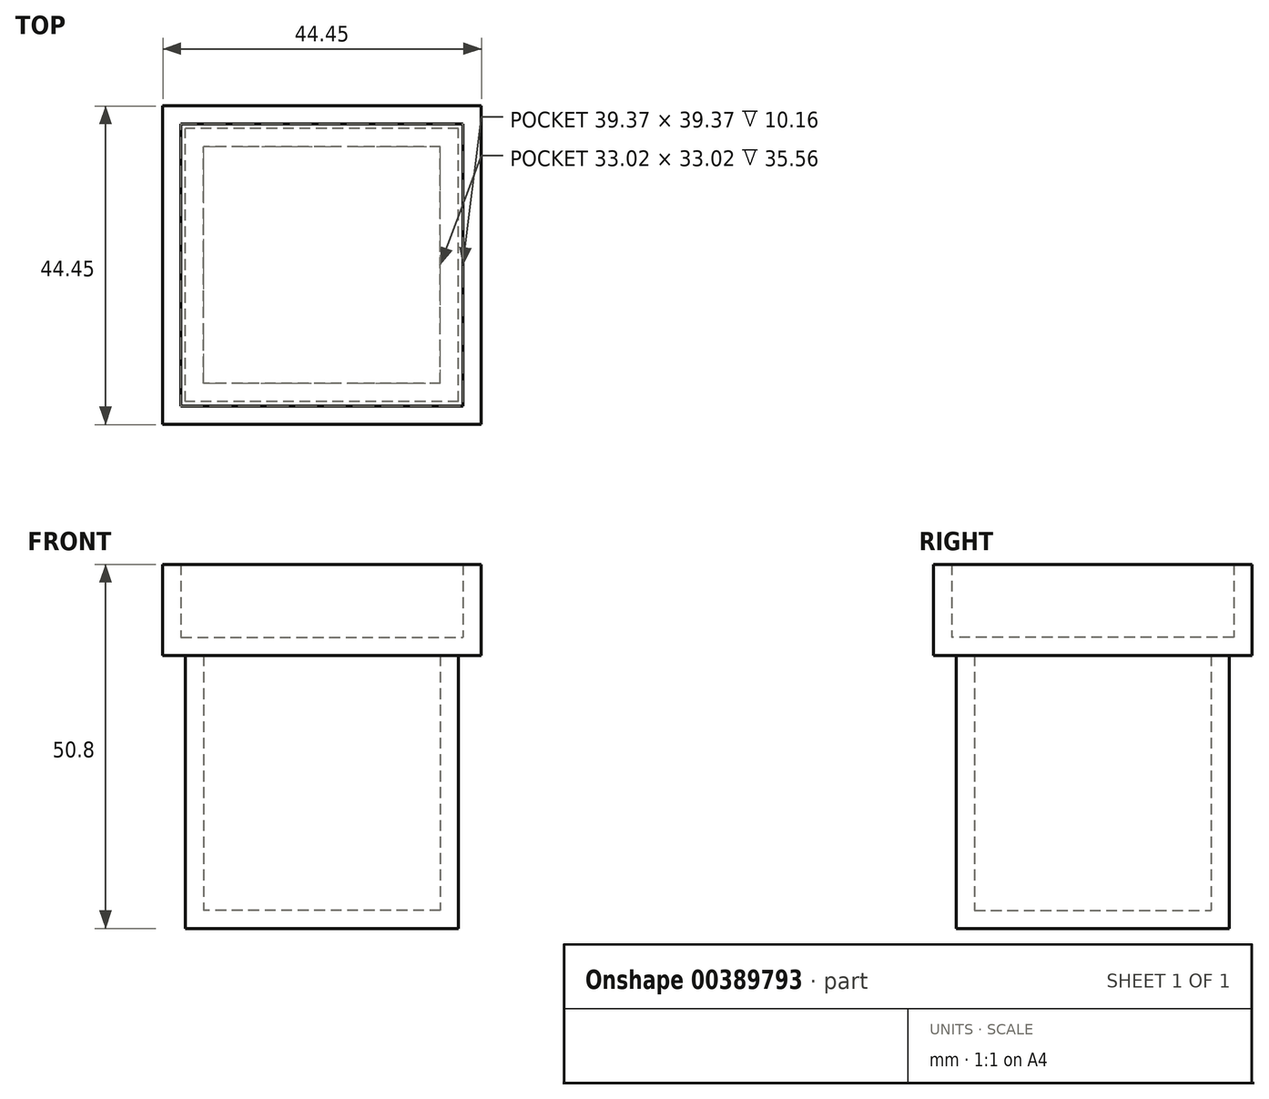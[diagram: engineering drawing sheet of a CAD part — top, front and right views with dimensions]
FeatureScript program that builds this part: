
annotation { "Feature Type Name" : "Feature", "Feature Type Description" : "" }
export const myFeature = defineFeature(function(context is Context, id is Id, definition is map)
    precondition{}
    {
        {
            var Q0;
            Q0=qCreatedBy(makeId("Top.planeOp"),FACE);
            var sketch = newSketch(context, id + "F0", { "sketchPlane" : qUnion([Q0])});
            skLineSegment(sketch, "E0.bottom", {"start": v(0, 0) * mm, "end": v(-38.1, 0) * mm});
            skLineSegment(sketch, "E0.top", {"start": v(0, 38.1) * mm, "end": v(-38.1, 38.1) * mm});
            skLineSegment(sketch, "E0.left", {"start": v(0, 0) * mm, "end": v(0, 38.1) * mm});
            skLineSegment(sketch, "E0.right", {"start": v(-38.1, 0) * mm, "end": v(-38.1, 38.1) * mm});
            skSolve(sketch);
        }
        {
            var Q0;
            Q0=makeQuery(id+"F0.imprint","IMPRINT",FACE,{"disambiguationData":[TD([[makeQuery(id+"F0.imprint","IMPRINT",EDGE,{"derivedFrom":sQuery(id+"F0.wireOp",EDGE,"E0.bottom")}),-1.0]])]});
            var sketch = newSketch(context, id + "F1", { "sketchPlane" : qUnion([Q0])});
            skSolve(sketch);
        }
        {
            var Q0;
            Q0=makeQuery(id+"F1.imprint","IMPRINT",FACE,{"disambiguationData":[TD([[makeQuery(id+"F1.imprint","IMPRINT",EDGE,{"derivedFrom":makeQuery(id+"F0.imprint","IMPRINT",EDGE,{"derivedFrom":sQuery(id+"F0.wireOp",EDGE,"E0.bottom")})}),-1.0]])]});
            extrude(context, id + "F2", {"entities" : qUnion([Q0]), "depth" : 38.1 * mm});
        }
        {
            var Q0;
            Q0=makeQuery(id+"F2.opExtrude","CAP_FACE",FACE,{"disambiguationData":[OSD([sQuery(id+"F0.wireOp",EDGE,"E0.bottom"),sQuery(id+"F0.wireOp",EDGE,"E0.top"),sQuery(id+"F0.wireOp",EDGE,"E0.left"),sQuery(id+"F0.wireOp",EDGE,"E0.right")])],"isStart":false});
            var sketch = newSketch(context, id + "F3", { "sketchPlane" : qUnion([Q0])});
            skLineSegment(sketch, "E1.0", {"start": v(-41.27, -3.18) * mm, "end": v(3.18, -3.18) * mm});
            skLineSegment(sketch, "E1.1", {"start": v(-41.28, 41.27) * mm, "end": v(-41.27, -3.18) * mm});
            skLineSegment(sketch, "E1.2", {"start": v(3.18, 41.27) * mm, "end": v(-41.28, 41.27) * mm});
            skLineSegment(sketch, "E1.3", {"start": v(3.18, -3.18) * mm, "end": v(3.18, 41.28) * mm});
            skSolve(sketch);
        }
        {
            var Q0;
            Q0 = qSketchRegion(id + "F3", true);
            extrude(context, id + "F4", {"entities" : qUnion([Q0]), "depth" : 12.7 * mm});
        }
        {
            var Q0;
            Q0=makeQuery(id+"F4.opExtrude","CAP_FACE",FACE,{"disambiguationData":[OSD([sQuery(id+"F3.wireOp",EDGE,"E1.0"),sQuery(id+"F3.wireOp",EDGE,"E1.1"),sQuery(id+"F3.wireOp",EDGE,"E1.2"),sQuery(id+"F3.wireOp",EDGE,"E1.3")])],"isStart":false});
            shell(context, id + "F5", {"entities" : qUnion([Q0]), "thickness" : 2.54 * mm});
        }
        {
            var Q0;
            Q0=makeQuery(id+"F2.opExtrude","CAP_FACE",FACE,{"disambiguationData":[OSD([sQuery(id+"F0.wireOp",EDGE,"E0.bottom"),sQuery(id+"F0.wireOp",EDGE,"E0.top"),sQuery(id+"F0.wireOp",EDGE,"E0.left"),sQuery(id+"F0.wireOp",EDGE,"E0.right")])],"isStart":false});
            shell(context, id + "F6", {"entities" : qUnion([Q0]), "thickness" : 2.54 * mm});
        }
    });
